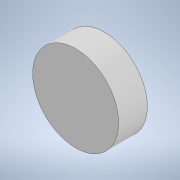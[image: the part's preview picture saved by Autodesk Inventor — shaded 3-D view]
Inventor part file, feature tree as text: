
AUTODESK INVENTOR PART (.ipt)
format: ipt  version: 2021.1 (Build 251245000, 245)  size: 123,904 bytes
history: native  units: in
note: dims shown in document units (in); Inventor stores cm internally (conversion verified against a paired STEP export)
features: extrude x3, sketch x3, fillet x1
ambient origin geometry x8: Origin, YZ Plane, XZ Plane, XY Plane, X Axis, Y Axis, Z Axis, Center Point
bodies: Solid1 (feature_tree)
feature tree (7):
  extrude  "Extrusion1"  Depth=0.125in
  extrude  "Extrusion2"  Depth=0.25in
  fillet  "Fillet1"  Radius=0.25in
  extrude  "Extrusion3"  Depth=0.25in
  sketch  "Sketch1"  dims[d0=1.25in d1=0.125in]
  sketch  "Sketch2"  dims[d2=0.25in d3=0.0in d4=0.05in d5=0.25in]
  sketch  "Sketch3"  dims[d6=0.0in d7=0.25in d8=0.4899in d9=0.25in d10=0.0in]
